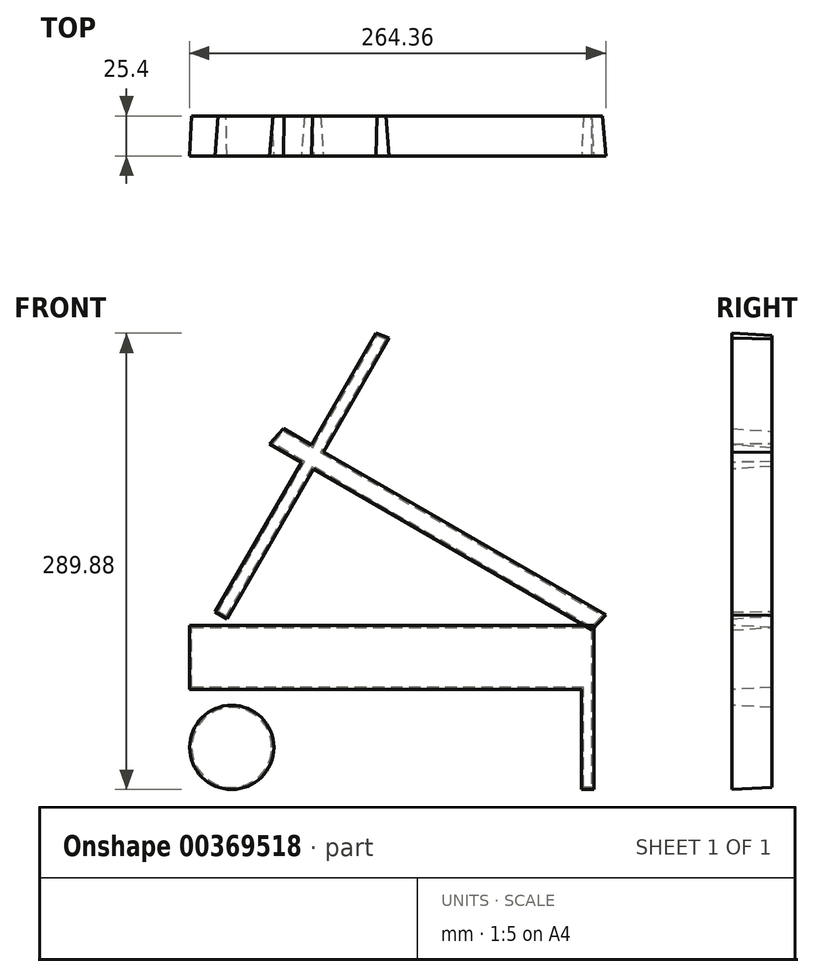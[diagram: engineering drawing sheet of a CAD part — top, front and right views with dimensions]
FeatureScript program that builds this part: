
annotation { "Feature Type Name" : "Feature", "Feature Type Description" : "" }
export const myFeature = defineFeature(function(context is Context, id is Id, definition is map)
    precondition{}
    {
        {
            var Q0;
            Q0=qCreatedBy(makeId("Front.planeOp"),FACE);
            var sketch = newSketch(context, id + "F0", { "sketchPlane" : qUnion([Q0])});
            skLineSegment(sketch, "E0.bottom", {"start": v(-170.32, -127.2) * mm, "end": v(83.68, -127.2) * mm});
            skLineSegment(sketch, "E0.top", {"start": v(-170.32, -89.1) * mm, "end": v(83.68, -89.1) * mm});
            skLineSegment(sketch, "E0.left", {"start": v(-170.32, -127.2) * mm, "end": v(-170.32, -89.1) * mm});
            skLineSegment(sketch, "E0.right", {"start": v(83.68, -127.2) * mm, "end": v(83.68, -89.1) * mm});
            skLineSegment(sketch, "E1", {"start": v(83.68, -89.1) * mm, "end": v(-118.78, 27.8) * mm});
            skLineSegment(sketch, "E2", {"start": v(-118.78, 27.8) * mm, "end": v(-111.85, 35.47) * mm});
            skLineSegment(sketch, "E3", {"start": v(-111.85, 35.47) * mm, "end": v(90.62, -81.43) * mm});
            skLineSegment(sketch, "E4", {"start": v(90.62, -81.43) * mm, "end": v(83.68, -89.1) * mm});
            skCircle(sketch, "E5", {"center": v(-144.92, -165.3) * mm, "radius": 25.4 * mm});
            skPoint(sketch, "E6.firstSnap0", {"position": v(83.68, -108.15) * mm});
            skLineSegment(sketch, "E6.bottom", {"start": v(83.68, -190.7) * mm, "end": v(78.6, -190.7) * mm});
            skLineSegment(sketch, "E6.top", {"start": v(83.68, -127.2) * mm, "end": v(78.6, -127.2) * mm});
            skLineSegment(sketch, "E6.left", {"start": v(83.68, -190.7) * mm, "end": v(83.68, -127.2) * mm});
            skLineSegment(sketch, "E6.right", {"start": v(78.6, -190.7) * mm, "end": v(78.6, -127.2) * mm});
            skLineSegment(sketch, "E7.bottom", {"start": v(-158.61, -81.9) * mm, "end": v(-145.91, -81.9) * mm});
            skLineSegment(sketch, "E7.top", {"start": v(-158.61, -89.1) * mm, "end": v(-145.91, -89.1) * mm});
            skLineSegment(sketch, "E7.left", {"start": v(-158.61, -81.9) * mm, "end": v(-158.61, -89.1) * mm});
            skLineSegment(sketch, "E7.right", {"start": v(-145.91, -81.9) * mm, "end": v(-145.91, -89.1) * mm});
            skLineSegment(sketch, "E8.bottom", {"start": v(-127.62, -127.2) * mm, "end": v(-102.22, -127.2) * mm});
            skLineSegment(sketch, "E9.bottom", {"start": v(-132.22, -139.9) * mm, "end": v(-157.62, -139.9) * mm});
            skLineSegment(sketch, "E9.top", {"start": v(-132.22, -127.2) * mm, "end": v(-157.62, -127.2) * mm});
            skLineSegment(sketch, "E9.left", {"start": v(-132.22, -139.9) * mm, "end": v(-132.22, -127.2) * mm});
            skLineSegment(sketch, "E9.right", {"start": v(-157.62, -139.9) * mm, "end": v(-157.62, -127.2) * mm});
            skLineSegment(sketch, "E10", {"start": v(-52.62, 96.2) * mm, "end": v(-153.7, -78.88) * mm});
            skLineSegment(sketch, "E11", {"start": v(-153.7, -78.88) * mm, "end": v(-148.45, -81.9) * mm});
            skLineSegment(sketch, "E12", {"start": v(-148.45, -81.9) * mm, "end": v(-46.85, 94.07) * mm});
            skLineSegment(sketch, "E13", {"start": v(-46.85, 94.07) * mm, "end": v(-52.62, 96.2) * mm});
            skSolve(sketch);
        }
        {
            var Q0;
            {var subQ2=sQuery(id+"F0.wireOp",EDGE,"E0.left");Q0=makeQuery(id+"F0.imprint","IMPRINT",FACE,{"disambiguationData":[TD([[makeQuery(id+"F0.imprint","IMPRINT",EDGE,{"derivedFrom":subQ2}),-1.0]])]});}
            var Q1;
            Q1=makeQuery(id+"F0.imprint","IMPRINT",FACE,{"disambiguationData":[TD([[makeQuery(id+"F0.imprint","IMPRINT",EDGE,{"derivedFrom":sQuery(id+"F0.wireOp",EDGE,"E7.top")}),1.0]])]});
            var Q2;
            {var subQ5=sQuery(id+"F0.wireOp",EDGE,"E11");Q2=makeQuery(id+"F0.imprint","IMPRINT",FACE,{"disambiguationData":[TD([[makeQuery(id+"F0.imprint","IMPRINT",EDGE,{"derivedFrom":subQ5}),1.0]])]});}
            var Q3;
            Q3=makeQuery(id+"F0.imprint","IMPRINT",FACE,{"disambiguationData":[TD([[makeQuery(id+"F0.imprint","IMPRINT",EDGE,{"derivedFrom":sQuery(id+"F0.wireOp",EDGE,"E9.top")}),1.0]])]});
            var Q4;
            Q4=makeQuery(id+"F0.imprint","IMPRINT",FACE,{"disambiguationData":[TD([[makeQuery(id+"F0.imprint","IMPRINT",EDGE,{"derivedFrom":sQuery(id+"F0.wireOp",EDGE,"E5")}),1.0]])]});
            var Q5;
            Q5=makeQuery(id+"F0.imprint","IMPRINT",FACE,{"disambiguationData":[TD([[makeQuery(id+"F0.imprint","IMPRINT",EDGE,{"derivedFrom":sQuery(id+"F0.wireOp",EDGE,"E6.bottom")}),-1.0]])]});
            var Q6;
            {var subQ0=sQuery(id+"F0.wireOp",EDGE,"E4");Q6=makeQuery(id+"F0.imprint","IMPRINT",FACE,{"disambiguationData":[TD([[makeQuery(id+"F0.imprint","IMPRINT",EDGE,{"derivedFrom":subQ0}),-1.0]])]});}
            var Q7;
            {var subQ0=sQuery(id+"F0.wireOp",EDGE,"E2");Q7=makeQuery(id+"F0.imprint","IMPRINT",FACE,{"disambiguationData":[TD([[makeQuery(id+"F0.imprint","IMPRINT",EDGE,{"derivedFrom":subQ0}),-1.0]])]});}
            var Q8;
            {var subQ5=sQuery(id+"F0.wireOp",EDGE,"E13");Q8=makeQuery(id+"F0.imprint","IMPRINT",FACE,{"disambiguationData":[TD([[makeQuery(id+"F0.imprint","IMPRINT",EDGE,{"derivedFrom":subQ5}),1.0]])]});}
            var Q9;
            {var subQ0=sQuery(id+"F0.wireOp",EDGE,"E10");var subQ1=sQuery(id+"F0.wireOp",EDGE,"E1");var subQ2=makeQuery(id+"F0.imprint","INTERSECT",VERTEX,{"derivedFrom":[subQ1,subQ0]});Q9=makeQuery(id+"F0.imprint","IMPRINT",FACE,{"disambiguationData":[TD([[makeQuery(id+"F0.imprint","IMPRINT",EDGE,{"disambiguationData":[TD([[subQ2,1.0]])],"derivedFrom":subQ1}),-1.0]])]});}
            extrude(context, id + "F1", {"entities" : qUnion([Q0, Q1, Q2, Q3, Q4, Q5, Q6, Q7, Q8, Q9]), "depth" : 25.4 * mm, "hasDraft" : true, "draftAngle" : 3 * degree});
        }
    });
